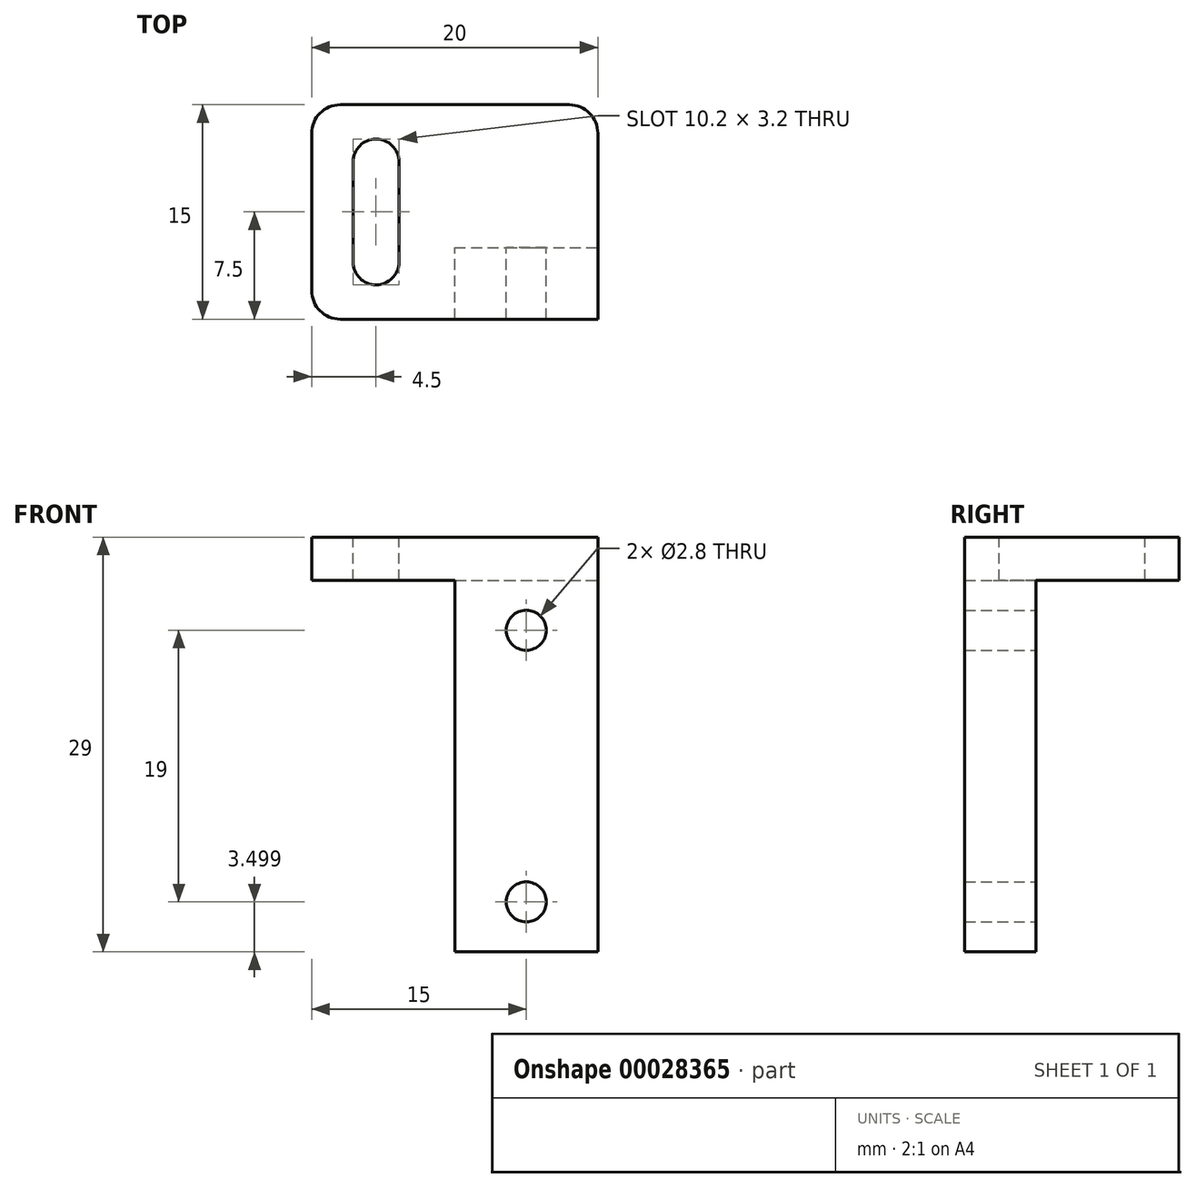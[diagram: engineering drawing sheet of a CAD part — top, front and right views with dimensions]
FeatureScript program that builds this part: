
annotation { "Feature Type Name" : "Feature", "Feature Type Description" : "" }
export const myFeature = defineFeature(function(context is Context, id is Id, definition is map)
    precondition{}
    {
        {
            var Q0;
            Q0=qCreatedBy(makeId("Front.planeOp"),FACE);
            var sketch = newSketch(context, id + "F0", { "sketchPlane" : qUnion([Q0])});
            skLineSegment(sketch, "E0.bottom", {"start": v(-2.41, 8.63) * mm, "end": v(7.59, 8.63) * mm});
            skLineSegment(sketch, "E0.top", {"start": v(-2.41, -20.37) * mm, "end": v(7.59, -20.37) * mm});
            skLineSegment(sketch, "E0.left", {"start": v(-2.41, 8.63) * mm, "end": v(-2.41, -20.37) * mm});
            skLineSegment(sketch, "E0.right", {"start": v(7.59, 8.63) * mm, "end": v(7.59, -20.37) * mm});
            skLineSegment(sketch, "E1.0", {"start": v(-2.41, 5.63) * mm, "end": v(5.59, 5.63) * mm, "construction": true});
            skSolve(sketch);
        }
        {
            var Q0;
            Q0=makeQuery(id+"F0.imprint","IMPRINT",FACE,{"disambiguationData":[TD([[makeQuery(id+"F0.imprint","IMPRINT",EDGE,{"derivedFrom":sQuery(id+"F0.wireOp",EDGE,"E0.bottom")}),-1.0]])]});
            extrude(context, id + "F1", {"entities" : qUnion([Q0]), "depth" : 5 * mm});
        }
        {
            var Q0;
            Q0=makeQuery(id+"F1.opExtrude","CAP_FACE",FACE,{"disambiguationData":[OSD([sQuery(id+"F0.wireOp",EDGE,"E0.bottom"),sQuery(id+"F0.wireOp",EDGE,"E0.top"),sQuery(id+"F0.wireOp",EDGE,"E0.left"),sQuery(id+"F0.wireOp",EDGE,"E0.right")])],"isStart":true});
            var sketch = newSketch(context, id + "F2", { "sketchPlane" : qUnion([Q0])});
            skLineSegment(sketch, "E2.0", {"start": v(-2.59, 9.63) * mm, "end": v(-2.59, -20.37) * mm, "construction": true});
            skCircle(sketch, "E3", {"center": v(-2.59, 2.13) * mm, "radius": 1.4 * mm});
            skCircle(sketch, "E4", {"center": v(-2.59, -16.87) * mm, "radius": 1.4 * mm});
            skLineSegment(sketch, "E5.0", {"start": v(2.41, -16.87) * mm, "end": v(-7.59, -16.87) * mm, "construction": true});
            skLineSegment(sketch, "E6.0", {"start": v(2.41, 2.13) * mm, "end": v(-7.59, 2.13) * mm, "construction": true});
            skSolve(sketch);
        }
        {
            var Q0;
            Q0=qSketchRegion(id+"F2",true);
            extrude(context, id + "F3", {"entities" : qUnion([Q0]), "operationType" : NewBodyOperationType.REMOVE, "oppositeDirection" : true, "depth" : 25 * mm});
        }
        {
            var Q0;
            Q0=makeQuery(id+"F1.opExtrude","SWEPT_FACE",FACE,{"disambiguationData":[OSD([sQuery(id+"F0.wireOp",EDGE,"E0.left")])]});
            var sketch = newSketch(context, id + "F4", { "sketchPlane" : qUnion([Q0])});
            skLineSegment(sketch, "E7.0", {"start": v(5, 5.63) * mm, "end": v(0, 5.63) * mm});
            skSolve(sketch);
        }
        {
            var Q0;
            Q0=qSketchRegion(id+"F4",true);
            var Q1;
            {var subQ2=sQuery(id+"F4.wireOp",EDGE,"E7.0");Q1=makeQuery(id+"F4.imprint","IMPRINT",FACE,{"disambiguationData":[TD([[makeQuery(id+"F4.imprint","IMPRINT",EDGE,{"derivedFrom":subQ2}),-1.0]])]});}
            extrude(context, id + "F5", {"entities" : qUnion([Q0, Q1]), "operationType" : NewBodyOperationType.ADD, "depth" : 10 * mm});
        }
        {
            var Q0;
            {var subQ0=sQuery(id+"F0.wireOp",EDGE,"E0.bottom");var subQ1=sQuery(id+"F0.wireOp",EDGE,"E0.left");var subQ2=makeQuery(id+"F1.opExtrude","CAP_EDGE",EDGE,{"disambiguationData":[OSD([subQ1])],"isStart":false});Q0=makeQuery(id+"F5.boolean.opBoolean","MERGE",FACE,{"derivedFrom":[makeQuery(id+"F1.opExtrude","CAP_FACE",FACE,{"disambiguationData":[OSD([subQ0,sQuery(id+"F0.wireOp",EDGE,"E0.top"),subQ1,sQuery(id+"F0.wireOp",EDGE,"E0.right")])],"isStart":false}),makeQuery(id+"F5.opExtrude","SWEPT_FACE",FACE,{"disambiguationData":[OSD([subQ1]),TDD([makeQuery(id+"F4.imprint","IMPRINT",EDGE,{"disambiguationData":[TD([[makeQuery(id+"F4.imprint","INTERSECT",VERTEX,{"derivedFrom":[subQ2,sQuery(id+"F4.wireOp",EDGE,"E7.0")]}),1.0]])],"derivedFrom":subQ2})])]})]});}
            var sketch = newSketch(context, id + "F6", { "sketchPlane" : qUnion([Q0])});
            skLineSegment(sketch, "E8", {"start": v(-2.41, 5.63) * mm, "end": v(7.59, 5.63) * mm});
            skSolve(sketch);
        }
        {
            var Q0;
            {var subQ1=sQuery(id+"F6.wireOp",EDGE,"E8");Q0=makeQuery(id+"F6.imprint","IMPRINT",FACE,{"disambiguationData":[TD([[makeQuery(id+"F6.imprint","IMPRINT",EDGE,{"derivedFrom":subQ1}),1.0]])]});}
            extrude(context, id + "F7", {"entities" : qUnion([Q0]), "operationType" : NewBodyOperationType.ADD, "oppositeDirection" : true, "depth" : 15 * mm});
        }
        {
            var Q0;
            {var subQ0=sQuery(id+"F0.wireOp",EDGE,"E0.bottom");var subQ1=sQuery(id+"F0.wireOp",EDGE,"E0.left");Q0=makeQuery(id+"F7.boolean.opBoolean","MERGE",FACE,{"derivedFrom":[makeQuery(id+"F5.boolean.opBoolean","MERGE",FACE,{"derivedFrom":[makeQuery(id+"F1.opExtrude","SWEPT_FACE",FACE,{"disambiguationData":[OSD([subQ0])]}),makeQuery(id+"F5.opExtrude","SWEPT_FACE",FACE,{"disambiguationData":[OSD([subQ0,subQ1])]})]}),makeQuery(id+"F7.opExtrude","SWEPT_FACE",FACE,{"disambiguationData":[OSD([subQ0,subQ1])]})]});}
            var sketch = newSketch(context, id + "F8", { "sketchPlane" : qUnion([Q0])});
            skLineSegment(sketch, "E9.0", {"start": v(-7.91, -10) * mm, "end": v(-7.91, 13.41) * mm, "construction": true});
            skLineSegment(sketch, "E10.0", {"start": v(-6.31, -1) * mm, "end": v(-6.31, 6) * mm});
            skLineSegment(sketch, "E11.0", {"start": v(-9.51, -1) * mm, "end": v(-9.51, 6) * mm});
            skLineSegment(sketch, "E12.0", {"start": v(-12.41, 6) * mm, "end": v(7.59, 6) * mm, "construction": true});
            skLineSegment(sketch, "E13.0", {"start": v(-12.41, -1) * mm, "end": v(7.59, -1) * mm, "construction": true});
            skArc(sketch, "E14", {"start": v(-9.51, 6) * mm, "mid": v(-7.91, 7.6) * mm, "end": v(-6.31, 6) * mm});
            skArc(sketch, "E15", {"start": v(-6.31, -1) * mm, "mid": v(-7.91, -2.6) * mm, "end": v(-9.51, -1) * mm});
            skSolve(sketch);
        }
        {
            var Q0;
            Q0=makeQuery(id+"F8.imprint","IMPRINT",FACE,{"disambiguationData":[TD([[makeQuery(id+"F8.imprint","IMPRINT",EDGE,{"derivedFrom":sQuery(id+"F8.wireOp",EDGE,"a678a36d-41d2-427d-8e55-0325338021f2.0")}),1.0]])]});
            var Q1;
            Q1=makeQuery(id+"F8.imprint","IMPRINT",FACE,{"disambiguationData":[TD([[makeQuery(id+"F8.imprint","IMPRINT",EDGE,{"derivedFrom":sQuery(id+"F8.wireOp",EDGE,"E10.0")}),1.0]])]});
            var Q2;
            Q2=sQuery(id+"F8.wireOp",EDGE,"a3b55649-b8dd-449b-a23e-8d3800de4019");
            var Q3;
            Q3=sQuery(id+"F8.wireOp",EDGE,"a678a36d-41d2-427d-8e55-0325338021f2.1");
            var Q4;
            Q4=sQuery(id+"F8.wireOp",EDGE,"a678a36d-41d2-427d-8e55-0325338021f2.0");
            var Q5;
            Q5=sQuery(id+"F8.wireOp",EDGE,"b0d7fb9c-0a67-47c0-9b60-9e4a61582d00");
            var Q6;
            Q6=sQuery(id+"F8.wireOp",EDGE,"8b5e1ef5-08ee-4b97-a625-3d02ef5d0c2a.0");
            var Q7;
            Q7=sQuery(id+"F8.wireOp",EDGE,"718d5cb8-3b57-48ea-b748-e179312c4179.0");
            extrude(context, id + "F9", {"entities" : qUnion([Q0, Q1]), "operationType" : NewBodyOperationType.REMOVE, "surfaceEntities" : qUnion([Q2, Q3, Q4, Q5, Q6, Q7]), "oppositeDirection" : true, "depth" : 25 * mm});
        }
        {
            var Q0;
            Q0=makeQuery(id+"F7.opExtrude","CAP_EDGE",EDGE,{"disambiguationData":[OSD([sQuery(id+"F0.wireOp",EDGE,"E0.right")])],"isStart":false});
            var Q1;
            Q1=makeQuery(id+"F7.opExtrude","CAP_EDGE",EDGE,{"disambiguationData":[OSD([sQuery(id+"F0.wireOp",EDGE,"E0.left")])],"isStart":false});
            var Q2;
            {var subQ0=sQuery(id+"F0.wireOp",EDGE,"E0.left");var subQ1=makeQuery(id+"F1.opExtrude","CAP_EDGE",EDGE,{"disambiguationData":[OSD([subQ0])],"isStart":false});Q2=makeQuery(id+"F5.opExtrude","CAP_EDGE",EDGE,{"disambiguationData":[OSD([subQ0]),TDD([makeQuery(id+"F4.imprint","IMPRINT",EDGE,{"disambiguationData":[TD([[makeQuery(id+"F4.imprint","INTERSECT",VERTEX,{"derivedFrom":[subQ1,sQuery(id+"F4.wireOp",EDGE,"E7.0")]}),1.0]])],"derivedFrom":subQ1})])],"isStart":false});}
            fillet(context, id + "F10", {"entities" : qUnion([Q0, Q1, Q2]), "radius" : 2 * mm, "tangentPropagation" : true, "allowEdgeOverflow" : false});
        }
    });
